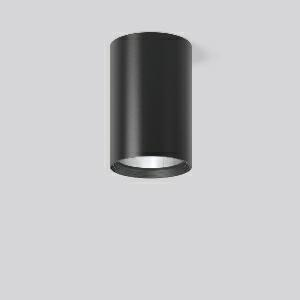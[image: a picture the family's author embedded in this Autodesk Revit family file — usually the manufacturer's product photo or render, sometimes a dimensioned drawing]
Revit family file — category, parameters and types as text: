
# Revit family: heledon_maxi_a_931225_003_2_b255
name_source: partatom
category: Lighting Fixtures
units: mm (PartAtom-declared; Revit-internal decimal feet)

## family parameters
Cut with Voids When Loaded = No
Host = Face
Light Source = No
Part Type = Normal
Room Calculation Point = No
Round Connector Dimension = Use Diameter
Shared = No

## types (1)
- HELEDON maxi A (1 x LED Modul 927, 4100 lm, 2700)
    Apparent Load = 35 VA
    Approval mark = CE
    CIE Flux Codes = 100 100 100 100 100
    Color Rendering = 92
    Color Temperature = 2700
    Default Elevation = 1800 mm
    Description = Series: HELEDON maxi
Cylindrical surface-mounted downlight. Housing: die-cast aluminium, powder-coated. Internal ceiling frame polycarbonate with bayonet mounting. Black plastic ring and recessed LED to prevent glare from the side. Optical assembly with reflector made of MIRO-Silver with 98% total light reflection for outstanding efficiency - can be changed without tools. Best colour rendering index Ra>90. Suitable for Ceiling mounting. Easy installation with a separate ceiling frame with bayonet mounting and plug connection. Driver integrated. Connected via plug-in connector. High quality converter without flickering and stroboscopic effect. The following accessories can be mounted without use of tools: interchangeable lenses, decorative glasses, honeycomb louvre, clear and frosted diffusers, white interchangeable plastic ring. 
Colour: deep black, matt (RAL 9005)
Diameter: 123 mm
Height: 183 mm
Lamp: LED
Socket: without socket
Colour temperature: 2700K
Colour rendering index (CRI): 92
System power: 35 W
Rated luminous flux: 4100 lm
Luminous efficiency: 117 lm/W
Control gear: Regulated power supply
Protection class: I
Type of protection: IP 20
    Height = 183 mm
    Lamp = 1 x LED Modul 927
    Lamp Light Flux = 4100 lm
    Lamp count = 1
    Length = 123 mm
    Lifetime = 50000 h
    Luminous efficacy = 117 lm/W
    Manufacturer = RZB
    ModVariant = No
    Model = 931225.003.2
    Mounting Place = Ceiling
    Mounting Type = Surface mounted
    Number of Poles = 1
    OnlyDefault = Yes
    Power Factor = 1
    Product Name = HELEDON maxi A
    Product group = Surface mounted downlights
    ProductGroupID = 302
    Protection Class = Protection class I
    Protection Degree = IP 20
    RLX_Detail_Level = 1
    RLX_Emergency_Light_Flux = 0 lm
    RLX_Emergency_Type = 0
    RLX_Emergency_Type_DB = No
    RlxData = <blob elided: 97269 chars, md5=f3bfda98>
    Socket = socket
    Standby Power = 0 W
    System Light Flux = 4100 lm
    System Power = 35 W
    Type Comments = Product without accessories
    Type Image = 931192.003.jpg
    URL = http://relux.com
    VarID = ---
    Voltage = 230 V
    Voltage Range = 220-240 V
    Weight = 0.00 kg
    Width = 0 mm  [stored 0 ft]

note: [stored X ft] marks values corroborated as IEEE doubles in the binary element streams (Revit-internal decimal feet)

## geometry (parser evidence)
native form markers: Blend x4, Sweep x10
no freeform markers — native parametric forms only
